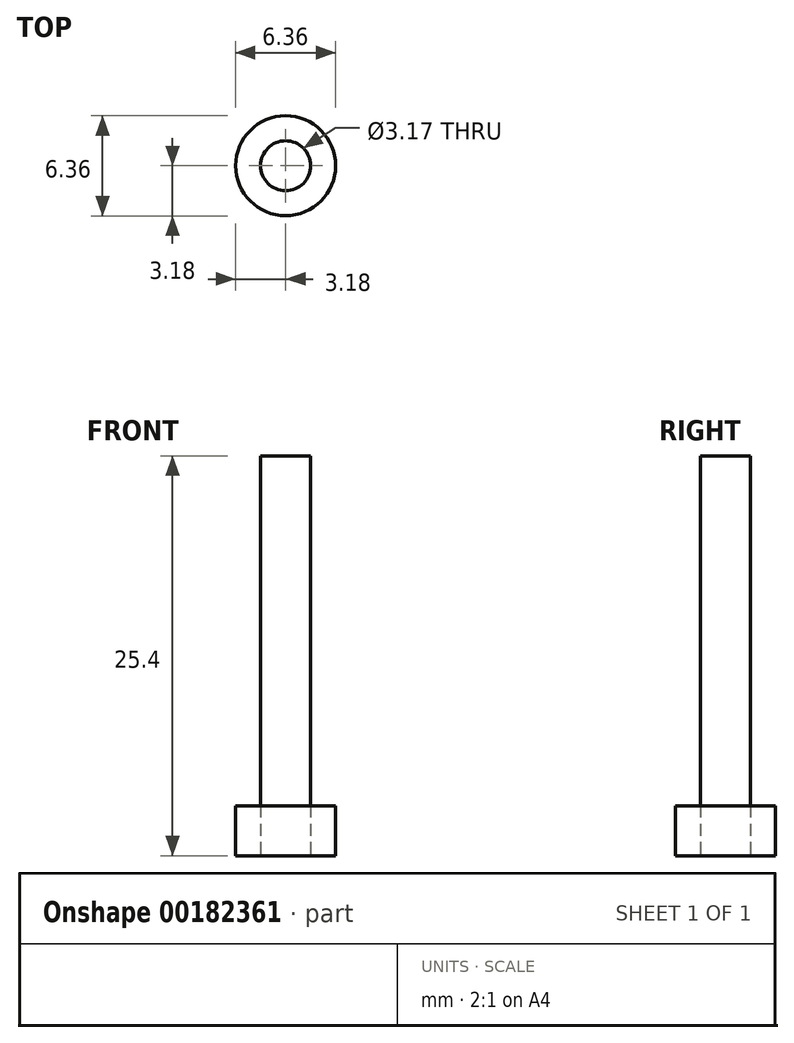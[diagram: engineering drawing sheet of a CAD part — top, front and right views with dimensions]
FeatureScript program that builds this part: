
annotation { "Feature Type Name" : "Feature", "Feature Type Description" : "" }
export const myFeature = defineFeature(function(context is Context, id is Id, definition is map)
    precondition{}
    {
        {
            var Q0;
            Q0=qCreatedBy(makeId("Top.planeOp"),FACE);
            var sketch = newSketch(context, id + "F0", { "sketchPlane" : qUnion([Q0])});
            skCircle(sketch, "E0", {"center": v(0, 0) * mm, "radius": 1.59 * mm});
            skSolve(sketch);
        }
        {
            var Q0;
            Q0 = qSketchRegion(id + "F0", true);
            extrude(context, id + "F1", {"entities" : qUnion([Q0]), "depth" : 25.4 * mm});
        }
        {
            var Q0;
            Q0=qCreatedBy(makeId("Top.planeOp"),FACE);
            var sketch = newSketch(context, id + "F2", { "sketchPlane" : qUnion([Q0])});
            skCircle(sketch, "E1", {"center": v(0, 0) * mm, "radius": 3.18 * mm});
            skCircle(sketch, "E2", {"center": v(0, 0) * mm, "radius": 1.59 * mm});
            skSolve(sketch);
        }
        {
            var Q0;
            Q0 = qSketchRegion(id + "F2", true);
            extrude(context, id + "F3", {"entities" : qUnion([Q0]), "operationType" : NewBodyOperationType.ADD, "depth" : 3.17 * mm});
        }
        {
            var Q0;
            Q0 = qSketchRegion(id + "F0", true);
            extrude(context, id + "F4", {"entities" : qUnion([Q0]), "operationType" : NewBodyOperationType.REMOVE, "depth" : 3.17 * mm});
        }
    });
